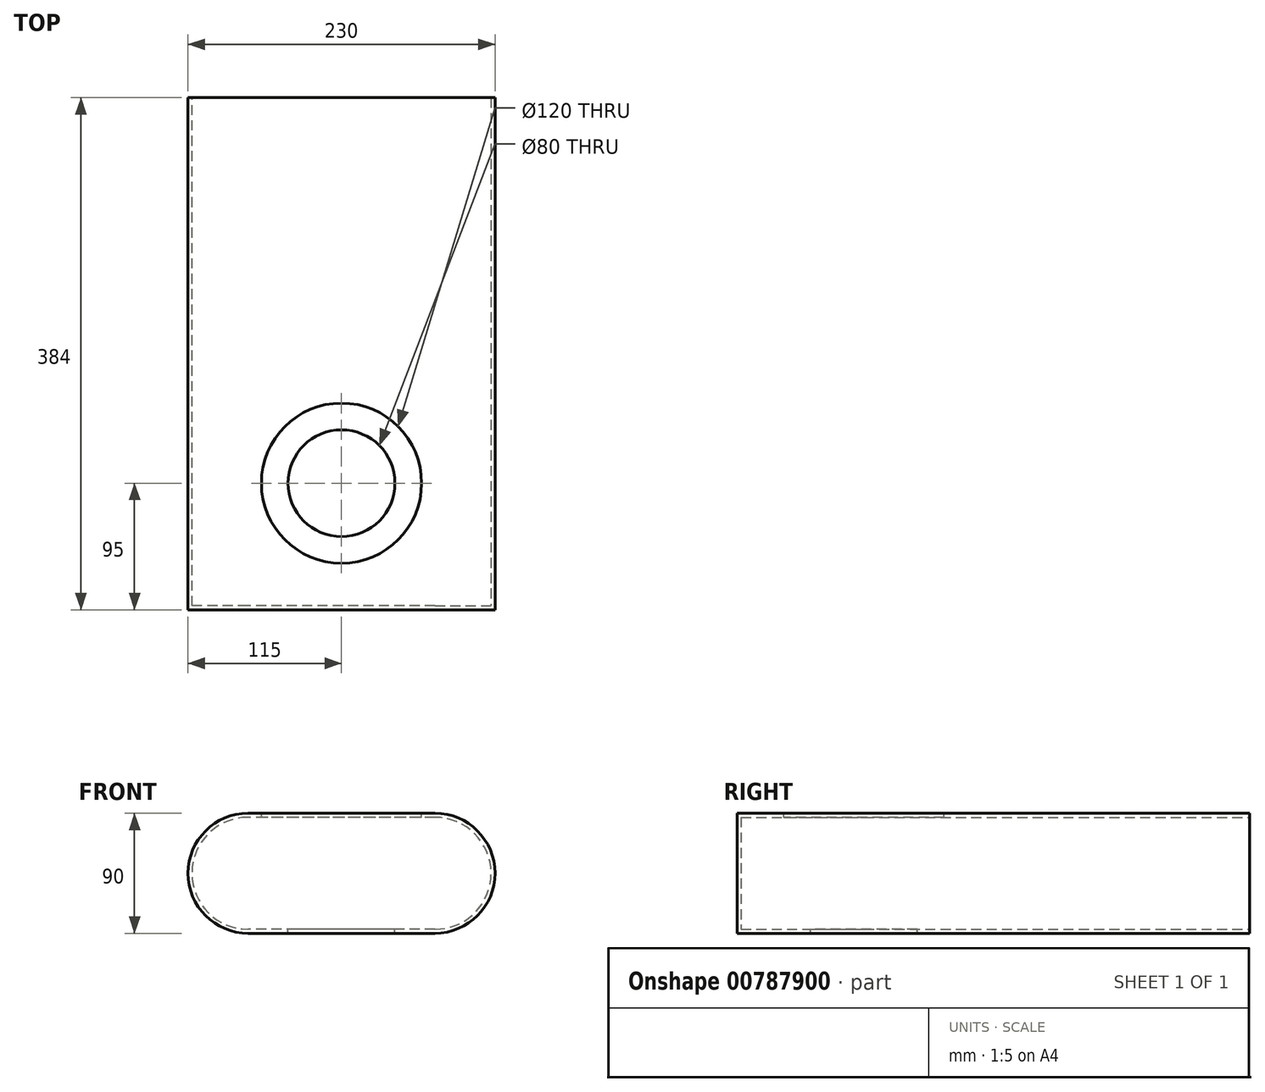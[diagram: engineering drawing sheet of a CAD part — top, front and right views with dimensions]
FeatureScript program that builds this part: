
annotation { "Feature Type Name" : "Feature", "Feature Type Description" : "" }
export const myFeature = defineFeature(function(context is Context, id is Id, definition is map)
    precondition{}
    {
        {
            var Q0;
            Q0=qCreatedBy(makeId("Top.planeOp"),FACE);
            var sketch = newSketch(context, id + "F0", { "sketchPlane" : qUnion([Q0])});
            skCircle(sketch, "E0", {"center": v(0, 0) * mm, "radius": 85 * mm, "construction": true});
            skLineSegment(sketch, "E1.bottom", {"start": v(115, -95) * mm, "end": v(-115, -95) * mm});
            skLineSegment(sketch, "E1.top", {"start": v(115, 289) * mm, "end": v(-115, 289) * mm});
            skLineSegment(sketch, "E1.left", {"start": v(115, -95) * mm, "end": v(115, 289) * mm});
            skLineSegment(sketch, "E1.right", {"start": v(-115, -95) * mm, "end": v(-115, 289) * mm});
            skPoint(sketch, "E2", {"position": v(0, -95) * mm});
            skSolve(sketch);
        }
        {
            var Q0;
            Q0 = qSketchRegion(id + "F0", true);
            extrude(context, id + "F1", {"entities" : qUnion([Q0]), "depth" : 90 * mm, "offsetDistance" : 25 * mm});
        }
        {
            var Q0;
            Q0=makeQuery(id+"F1.opExtrude","CAP_EDGE",EDGE,{"disambiguationData":[OSD([sQuery(id+"F0.wireOp",EDGE,"E1.right")])],"isStart":false});
            var Q1;
            Q1=makeQuery(id+"F1.opExtrude","CAP_EDGE",EDGE,{"disambiguationData":[OSD([sQuery(id+"F0.wireOp",EDGE,"E1.left")])],"isStart":false});
            var Q2;
            Q2=makeQuery(id+"F1.opExtrude","CAP_EDGE",EDGE,{"disambiguationData":[OSD([sQuery(id+"F0.wireOp",EDGE,"E1.right")])],"isStart":true});
            var Q3;
            Q3=makeQuery(id+"F1.opExtrude","CAP_EDGE",EDGE,{"disambiguationData":[OSD([sQuery(id+"F0.wireOp",EDGE,"E1.left")])],"isStart":true});
            fillet(context, id + "F2", {"entities" : qUnion([Q0, Q1, Q2, Q3]), "radius" : 45 * mm, "tangentPropagation" : true, "allowEdgeOverflow" : false});
        }
        {
            var Q0;
            {var subQ0=sQuery(id+"F0.wireOp",EDGE,"E1.top");Q0=makeQuery(id+"F1.boolean.opBoolean","MERGE",FACE,{"derivedFrom":[makeQuery(id+"FuDmxqLo9UL07it_0.opExtrude","SWEPT_FACE",FACE,{"disambiguationData":[OSD([subQ0])]}),makeQuery(id+"F1.opExtrude","SWEPT_FACE",FACE,{"disambiguationData":[OSD([subQ0])]})]});}
            shell(context, id + "F3", {"entities" : qUnion([Q0]), "thickness" : 3 * mm});
        }
        {
            var Q0;
            Q0=makeQuery(id+"F1.opExtrude","CAP_FACE",FACE,{"disambiguationData":[OSD([sQuery(id+"F0.wireOp",EDGE,"E1.bottom"),sQuery(id+"F0.wireOp",EDGE,"E1.top"),sQuery(id+"F0.wireOp",EDGE,"E1.left"),sQuery(id+"F0.wireOp",EDGE,"E1.right")])],"isStart":false});
            var sketch = newSketch(context, id + "F4", { "sketchPlane" : qUnion([Q0])});
            skCircle(sketch, "E3", {"center": v(0, 0) * mm, "radius": 60 * mm});
            skCircle(sketch, "E4", {"center": v(0, 0) * mm, "radius": 40 * mm});
            skSolve(sketch);
        }
        {
            var Q0;
            Q0=makeQuery(id+"F4.imprint","IMPRINT",FACE,{"disambiguationData":[TD([[makeQuery(id+"F4.imprint","IMPRINT",EDGE,{"derivedFrom":sQuery(id+"F4.wireOp",EDGE,"E3")}),1.0]])]});
            extrude(context, id + "F5", {"entities" : qUnion([Q0]), "operationType" : NewBodyOperationType.REMOVE, "endBound" : BoundingType.UP_TO_NEXT, "oppositeDirection" : true, "depth" : 25 * mm, "offsetDistance" : 25 * mm});
        }
        {
            var Q0;
            Q0=makeQuery(id+"F4.imprint","IMPRINT",FACE,{"disambiguationData":[TD([[makeQuery(id+"F4.imprint","IMPRINT",EDGE,{"derivedFrom":sQuery(id+"F4.wireOp",EDGE,"E4")}),1.0]])]});
            extrude(context, id + "F6", {"entities" : qUnion([Q0]), "operationType" : NewBodyOperationType.REMOVE, "endBound" : BoundingType.THROUGH_ALL, "oppositeDirection" : true, "depth" : 25 * mm, "offsetDistance" : 25 * mm});
        }
    });
